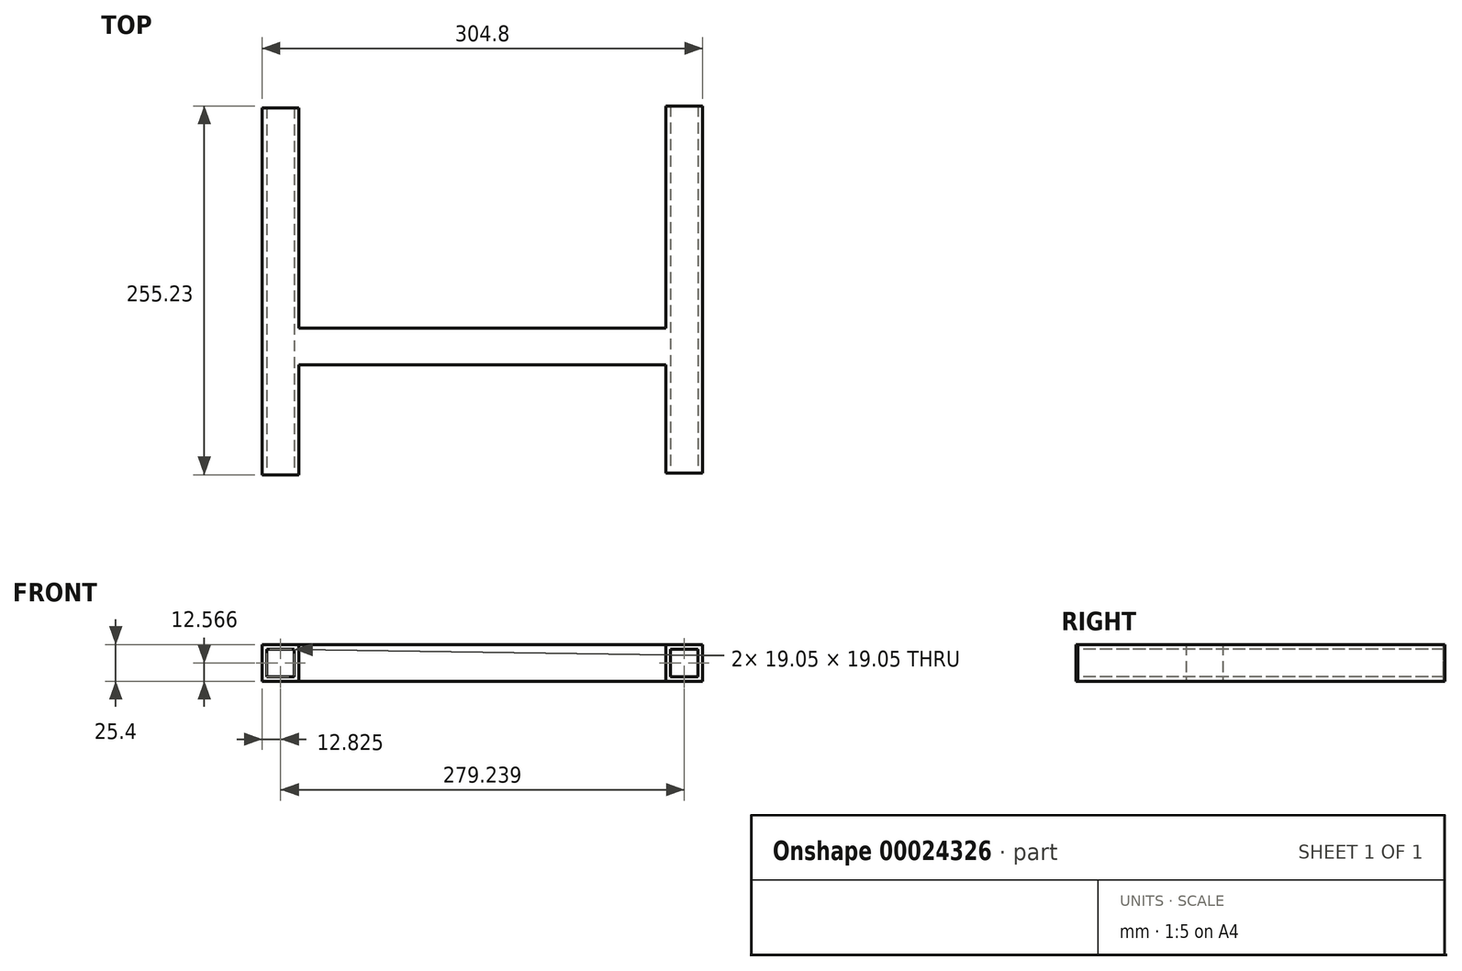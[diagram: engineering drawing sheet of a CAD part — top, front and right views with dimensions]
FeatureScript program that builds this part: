
annotation { "Feature Type Name" : "Feature", "Feature Type Description" : "" }
export const myFeature = defineFeature(function(context is Context, id is Id, definition is map)
    precondition{}
    {
        {
            var Q0;
            Q0=qCreatedBy(makeId("Top.planeOp"),FACE);
            var sketch = newSketch(context, id + "F0", { "sketchPlane" : qUnion([Q0])});
            skLineSegment(sketch, "E0", {"start": v(-47.02, 152.4) * mm, "end": v(-21.62, 152.4) * mm});
            skLineSegment(sketch, "E1", {"start": v(-21.62, 152.4) * mm, "end": v(-21.62, 0) * mm});
            skLineSegment(sketch, "E2", {"start": v(-21.62, 0) * mm, "end": v(232.38, 0) * mm});
            skLineSegment(sketch, "E3", {"start": v(232.38, 0) * mm, "end": v(232.38, 153.63) * mm});
            skLineSegment(sketch, "E4", {"start": v(232.38, 153.63) * mm, "end": v(257.78, 153.63) * mm});
            skLineSegment(sketch, "E5", {"start": v(257.78, 153.63) * mm, "end": v(257.78, -100.37) * mm});
            skLineSegment(sketch, "E6", {"start": v(257.78, -100.37) * mm, "end": v(232.38, -100.37) * mm});
            skLineSegment(sketch, "E7", {"start": v(232.38, -100.37) * mm, "end": v(232.38, -25.4) * mm});
            skLineSegment(sketch, "E8", {"start": v(232.38, -25.4) * mm, "end": v(-21.62, -25.4) * mm});
            skLineSegment(sketch, "E9", {"start": v(-21.62, -25.4) * mm, "end": v(-21.62, -101.6) * mm});
            skLineSegment(sketch, "E10", {"start": v(-21.62, -101.6) * mm, "end": v(-47.02, -101.6) * mm});
            skLineSegment(sketch, "E11", {"start": v(-47.02, -101.6) * mm, "end": v(-47.02, 152.4) * mm});
            skLineSegment(sketch, "E12", {"start": v(-47.02, -63.06) * mm, "end": v(-47.02, 25.4) * mm});
            skSolve(sketch);
        }
        {
            var Q0;
            {var subQ0=sQuery(id+"F0.wireOp",EDGE,"E0");Q0=makeQuery(id+"F0.imprint","IMPRINT",FACE,{"disambiguationData":[TD([[makeQuery(id+"F0.imprint","IMPRINT",EDGE,{"derivedFrom":subQ0}),-1.0]])]});}
            extrude(context, id + "F1", {"entities" : qUnion([Q0]), "depth" : 25.4 * mm});
        }
        {
            var Q0;
            Q0=makeQuery(id+"F1.opExtrude","SWEPT_FACE",FACE,{"disambiguationData":[OSD([sQuery(id+"F0.wireOp",EDGE,"E10")])]});
            var sketch = newSketch(context, id + "F2", { "sketchPlane" : qUnion([Q0])});
            skLineSegment(sketch, "E13", {"start": v(-43.72, 3.04) * mm, "end": v(-24.67, 3.04) * mm});
            skLineSegment(sketch, "E14", {"start": v(-24.67, 3.04) * mm, "end": v(-24.67, 22.1) * mm});
            skLineSegment(sketch, "E15", {"start": v(-24.67, 22.1) * mm, "end": v(-43.72, 22.1) * mm});
            skLineSegment(sketch, "E16", {"start": v(-43.72, 3.04) * mm, "end": v(-43.72, 22.1) * mm});
            skSolve(sketch);
        }
        {
            var Q0;
            Q0=makeQuery(id+"F2.imprint","IMPRINT",FACE,{"disambiguationData":[TD([[makeQuery(id+"F2.imprint","IMPRINT",EDGE,{"derivedFrom":sQuery(id+"F2.wireOp",EDGE,"E13")}),1.0]])]});
            extrude(context, id + "F3", {"entities" : qUnion([Q0]), "operationType" : NewBodyOperationType.REMOVE, "oppositeDirection" : true, "depth" : 266.55 * mm});
        }
        {
            var Q0;
            Q0=makeQuery(id+"F1.opExtrude","SWEPT_FACE",FACE,{"disambiguationData":[OSD([sQuery(id+"F0.wireOp",EDGE,"E6")])]});
            var sketch = newSketch(context, id + "F4", { "sketchPlane" : qUnion([Q0])});
            skLineSegment(sketch, "E17", {"start": v(254.57, 3.13) * mm, "end": v(254.57, 22.18) * mm});
            skLineSegment(sketch, "E18", {"start": v(254.57, 22.18) * mm, "end": v(235.52, 22.18) * mm});
            skLineSegment(sketch, "E19", {"start": v(235.52, 22.18) * mm, "end": v(235.52, 3.13) * mm});
            skLineSegment(sketch, "E20", {"start": v(235.52, 3.13) * mm, "end": v(254.57, 3.13) * mm});
            skSolve(sketch);
        }
        {
            var Q0;
            Q0=makeQuery(id+"F4.imprint","IMPRINT",FACE,{"disambiguationData":[TD([[makeQuery(id+"F4.imprint","IMPRINT",EDGE,{"derivedFrom":sQuery(id+"F4.wireOp",EDGE,"E17")}),1.0]])]});
            extrude(context, id + "F5", {"entities" : qUnion([Q0]), "operationType" : NewBodyOperationType.REMOVE, "oppositeDirection" : true, "depth" : 256.48 * mm});
        }
    });
